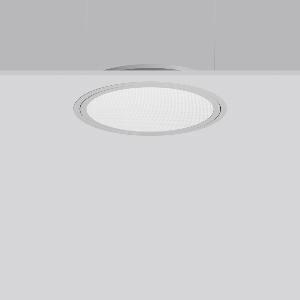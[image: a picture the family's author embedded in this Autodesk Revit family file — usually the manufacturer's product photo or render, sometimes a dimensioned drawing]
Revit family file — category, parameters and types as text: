
# Revit family: triona_round_e_312423_004_12_ecfb
name_source: partatom
category: Lighting Fixtures
units: mm (PartAtom-declared; Revit-internal decimal feet)

## family parameters
Cut with Voids When Loaded = No
Host = Face
Light Source = No
Part Type = Normal
Room Calculation Point = No
Round Connector Dimension = Use Diameter
Shared = No

## types (1)
- TRIONA round E (1 x LED Modul 830, 3150 lm, 3000)
    Apparent Load = 28 VA
    CIE Flux Codes = 58 87 97 100 100
    Color Rendering = 80
    Color Temperature = 3000
    Default Elevation = 1800 mm
    Description = Series: TRIONA round
Decorative round LED recessed surface luminaire. Cover made of sheet steel, powder-coated. Frame made of aluminium, powder-coated. Recessed ring: aluminium extrusion profile, powder coated. Light emission through a diffuser in plastic, opal/prismatic. Lightguide and diffuser made of non-yellowing plastic (PMMA). Lateral light emission (RZB SIDELITE technology) for above-average homogeneous light distribution. Suitable for installation in cavity ceilings. Tool-free mounting system thanks to the rocker arm mechanism (patent pending). Electronic ballast included. Very easy installation thanks to Plug+Play connection. 
Colour: silver, matt (approx. RAL 9006)
Diameter: 505 mm
Height: 2 mm
Cut-out diameter: 482 mm
Recess height: 100 mm
Luminaire: recess height: 89 mm
Lamp: LED
Socket: without socket
Colour temperature: 3000K
Colour rendering index (CRI): 80
System power: 28 W
Rated luminous flux: 3150 lm
Luminous efficiency: 113 lm/W
Control gear: Converter, dimmable, DALI
Protection class: I
Type of protection: IP 40
    Height = 0 mm  [stored 0 ft]
    Lamp = 1 x LED Modul 830
    Lamp Light Flux = 3150 lm
    Lamp count = 1
    Length = 505 mm
    Lifetime = 50000 h
    Luminous efficacy = 113 lm/W
    Manufacturer = RZB
    ModVariant = No
    Model = 312423.004.12
    Mounting Place = Ceiling
    Mounting Type = Recessed
    Number of Poles = 1
    OnlyDefault = Yes
    Power Factor = 1
    Product Name = TRIONA round E
    Product group = Recessed modular luminaires
    ProductGroupID = 406
    Protection Class = Protection class I
    Protection Degree = IP 20
    RLX_Detail_Level = 1
    RLX_Emergency_Light_Flux = 0 lm
    RLX_Emergency_Type = 0
    RLX_Emergency_Type_DB = No
    RlxData = <blob elided: 31593 chars, md5=71dbd520>
    Socket = socket
    Standby Power = 0 W
    System Light Flux = 3150 lm
    System Power = 28 W
    Type Comments = Product without accessories
    Type Image = 312423.004.12.jpg
    URL = http://relux.com
    VarID = ---
    Voltage = 230 V
    Voltage Range = 220-240 V
    Weight = 0.00 kg
    Width = 0 mm  [stored 0 ft]

note: [stored X ft] marks values corroborated as IEEE doubles in the binary element streams (Revit-internal decimal feet)

## geometry (parser evidence)
native form markers: Blend x4, Sweep x10
no freeform markers — native parametric forms only
